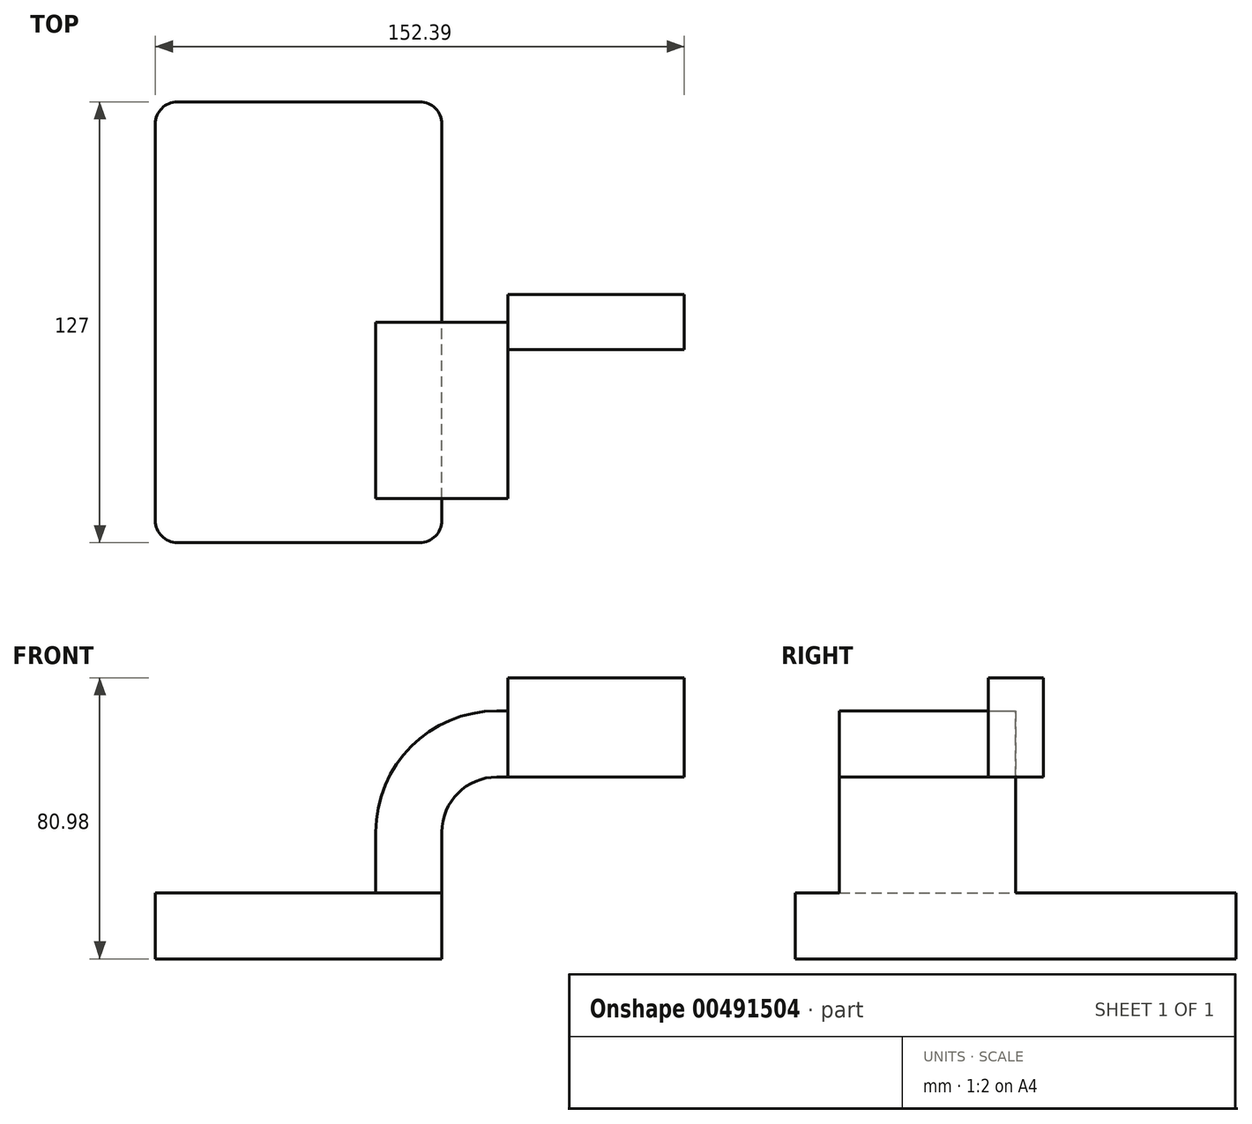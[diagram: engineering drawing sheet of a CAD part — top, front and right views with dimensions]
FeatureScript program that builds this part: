
annotation { "Feature Type Name" : "Feature", "Feature Type Description" : "" }
export const myFeature = defineFeature(function(context is Context, id is Id, definition is map)
    precondition{}
    {
        {
            var Q0;
            Q0=qCreatedBy(makeId("Front.planeOp"),FACE);
            var sketch = newSketch(context, id + "F0", { "sketchPlane" : qUnion([Q0])});
            skLineSegment(sketch, "E0.bottom", {"start": v(-41.28, -9.53) * mm, "end": v(41.28, -9.53) * mm});
            skLineSegment(sketch, "E0.top", {"start": v(-41.28, 9.53) * mm, "end": v(41.28, 9.53) * mm});
            skLineSegment(sketch, "E0.left", {"start": v(-41.28, -9.53) * mm, "end": v(-41.28, 9.53) * mm});
            skLineSegment(sketch, "E0.right", {"start": v(41.28, -9.53) * mm, "end": v(41.28, 9.52) * mm});
            skPoint(sketch, "E0.middle", {"position": v(0, 0) * mm});
            skLineSegment(sketch, "E1.bottom", {"start": v(111.12, 42.88) * mm, "end": v(60.33, 42.88) * mm});
            skLineSegment(sketch, "E1.top", {"start": v(111.12, 71.45) * mm, "end": v(60.33, 71.45) * mm});
            skLineSegment(sketch, "E1.left", {"start": v(111.12, 42.88) * mm, "end": v(111.12, 71.45) * mm});
            skLineSegment(sketch, "E1.right", {"start": v(60.33, 42.88) * mm, "end": v(60.33, 71.45) * mm});
            skPoint(sketch, "E1.middle", {"position": v(85.72, 57.16) * mm});
            skLineSegment(sketch, "E2", {"start": v(41.28, 9.52) * mm, "end": v(41.28, 27) * mm});
            skArc(sketch, "E3", {"start": v(41.27, 27) * mm, "mid": v(45.92, 38.23) * mm, "end": v(57.15, 42.88) * mm});
            skLineSegment(sketch, "E4", {"start": v(57.15, 42.88) * mm, "end": v(85.72, 42.88) * mm});
            skLineSegment(sketch, "E5.0", {"start": v(57.15, 61.93) * mm, "end": v(85.72, 61.93) * mm});
            skArc(sketch, "E5.1", {"start": v(22.23, 27) * mm, "mid": v(32.45, 51.7) * mm, "end": v(57.15, 61.93) * mm});
            skLineSegment(sketch, "E5.2", {"start": v(22.22, 9.52) * mm, "end": v(22.22, 27) * mm});
            skFitSpline(sketch, "E6", {"points": [v(-41.28, 9.53) * mm, v(-9.1, 29.66) * mm, v(57.15, 61.93) * mm], "startDerivative": vector(-13.63, 410.3) * mm, "endDerivative": vector(236.98, -57.74) * mm});
            skSolve(sketch);
        }
        {
            var Q0;
            Q0=makeQuery(id+"F0.imprint","IMPRINT",FACE,{"disambiguationData":[TD([[makeQuery(id+"F0.imprint","IMPRINT",EDGE,{"derivedFrom":sQuery(id+"F0.wireOp",EDGE,"E0.bottom")}),1.0]])]});
            extrude(context, id + "F1", {"entities" : qUnion([Q0]), "endBound" : BoundingType.SYMMETRIC, "depth" : 127 * mm});
        }
        {
            var Q0;
            Q0=makeQuery(id+"F0.imprint","IMPRINT",FACE,{"disambiguationData":[TD([[makeQuery(id+"F0.imprint","IMPRINT",EDGE,{"derivedFrom":sQuery(id+"F0.wireOp",EDGE,"E5.1")}),1.0]])]});
            extrude(context, id + "F2", {"entities" : qUnion([Q0]), "operationType" : NewBodyOperationType.ADD, "depth" : 50.8 * mm});
        }
        {
            var Q0;
            {var subQ5=sQuery(id+"F0.wireOp",EDGE,"E1.bottom");Q0=makeQuery(id+"F0.imprint","IMPRINT",FACE,{"disambiguationData":[TD([[makeQuery(id+"F0.imprint","IMPRINT",EDGE,{"derivedFrom":subQ5}),-1.0]])]});}
            extrude(context, id + "F3", {"entities" : qUnion([Q0]), "endBound" : BoundingType.SYMMETRIC, "depth" : 15.88 * mm});
        }
        {
            var Q0;
            Q0=makeQuery(id+"F1.opExtrude","CAP_EDGE",EDGE,{"disambiguationData":[OSD([sQuery(id+"F0.wireOp",EDGE,"E0.left")])],"isStart":false});
            var Q1;
            Q1=makeQuery(id+"F1.opExtrude","CAP_EDGE",EDGE,{"disambiguationData":[OSD([sQuery(id+"F0.wireOp",EDGE,"E0.right")])],"isStart":false});
            var Q2;
            Q2=makeQuery(id+"F1.opExtrude","CAP_EDGE",EDGE,{"disambiguationData":[OSD([sQuery(id+"F0.wireOp",EDGE,"E0.right")])],"isStart":true});
            var Q3;
            Q3=makeQuery(id+"F1.opExtrude","CAP_EDGE",EDGE,{"disambiguationData":[OSD([sQuery(id+"F0.wireOp",EDGE,"E0.left")])],"isStart":true});
            fillet(context, id + "F4", {"entities" : qUnion([Q0, Q1, Q2, Q3]), "radius" : 6.35 * mm, "tangentPropagation" : true, "allowEdgeOverflow" : false});
        }
    });
